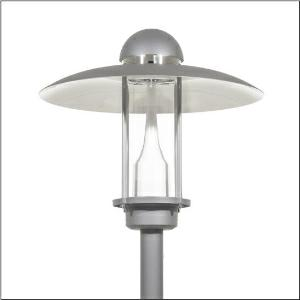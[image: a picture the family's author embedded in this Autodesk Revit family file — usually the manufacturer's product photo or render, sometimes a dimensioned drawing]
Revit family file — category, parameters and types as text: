
# Revit family: city-light_elegance_iq___st1_2a_5xa5265mf14h_1b27
name_source: partatom
category: Lighting Fixtures
units: mm (PartAtom-declared; Revit-internal decimal feet)

## family parameters
Cut with Voids When Loaded = No
Host = Face
Light Source = No
Part Type = Normal
Room Calculation Point = No
Round Connector Dimension = Use Diameter
Shared = No

## types (1)
- --- (1 x LED, 1470 lm, 11.8 W, 2700K)
    Apparent Load = 12 VA
    CIE Flux Codes = 22 62 94 98 100
    Color Rendering = 70
    Color Temperature = 2700K
    Default Elevation = 1800 mm
    Description = City-Light Elegance iQ, mast luminaire, Module 540 iQ-SR, primary light control with 3 zone facetted reflector, of plastic, silver coated, highly specular, structured, primary optical cover: cover, of PMMA, transparent, light distribution: ST1.2a, light emission: direct distribution, primary light characteristic: asymmetric, installation type: post-top, LED, High Power LED, rated luminous flux: 1.470lm, luminous efficacy: 124lm/W, light colour: 727, colour temperature: 2700K, control gear: ECG iQ, control: presetting dimming logarithmic, Street-Remote, Auto-Match, Temp-Guard, Lumen-Switch, Night-Set, Smart-Wire, Light-Fading, Desk-Remote (wireless, voltage-free reading and setting of iQ features in the workshop via application-optimized NFC function/RFID function), optimised constant luminous flux control (CLO 2.0), with terminal, 6-pole, max. 2.5mm², mains connection: 230..240V, AC, 50/60Hz, start of lifetime: 12W, end of service life: 12W, reduction: 6W, luminaire housing, upper part, of aluminium, coated, Siteco® metallic grey (DB 702S), diameter: 750mm, height: 675mm, spigot size: d x l = 76 x 70mm (post-top) | with reducer (optional accessory) 60 x 70mm, post-top mast mounting element, of diecast aluminium, coated, Siteco® metallic grey (DB 702S), Module 540 iQ-SR, traffic white (RAL 9016), equipment: standard, protection rating (complete): IP65, insulation class (complete): insulation class II (safety insulation), certification: CE, ENEC, VDE, packaging unit: 1 piece

Light Distribution: ST1.2a
    Height = 675 mm
    Lamp = 1 x LED
    Lamp Light Flux = 1470 lm
    Lamp Power = 11.8 W
    Lamp count = 1
    Length = 750 mm
    Luminous efficacy = 125 lm/W
    Manufacturer = Siteco
    ModVariant = No
    Model = 5XA5265MF14H
    Number of Poles = 1
    OnlyDefault = Yes
    Power Factor = 1
    Product Name = City-Light Elegance iQ | ST1.2a
    Product group = mast luminaire | pylon top
    ProductGroupID = 6100
    Protection Class = Protection class II
    Protection Degree = IP 65
    RLX_Detail_Level = 1
    RLX_Emergency_Light_Flux = 0 lm
    RLX_Emergency_Type = 0
    RLX_Emergency_Type_DB = No
    RlxData = <blob elided: 99933 chars, md5=d738a3e6>
    Socket = socket
    Standby Power = 0 W
    System Light Flux = 1470 lm
    System Power = 12 W
    Type Comments = factory setting: luminous flux: 100 % | dim-lin: 254 | 472 mA
    Type Image = l_1006912.jpg
    URL = http://relux.com
    VarID = @adj_103403
    Voltage = 0 V
    Weight = 0.00 kg
    Width = 0 mm  [stored 0 ft]

note: [stored X ft] marks values corroborated as IEEE doubles in the binary element streams (Revit-internal decimal feet)

## geometry (parser evidence)
native form markers: Blend x4, Sweep x11
no freeform markers — native parametric forms only
